# Revit family: E_Actuator_F_MEPcontent_Oventrop_Aktor M ST 2P 3P L Square Law
name_source: partatom
category: Electrical Fixtures
revit_build: Autodesk Revit MEP 2015 (Build: 20140606_1530(x64)
units: mm (PartAtom-declared; Revit-internal decimal feet)

## types (3) — shared parameters
Ambient Temperature = -10 °C up to +55 °C
Black = Color RGB 060-060-060
Content Supplier URL = www.mepcontent.eu
Custom = No
Default Elevation = 1219.2 mm  [stored 4 ft]
Drive = 0–10 V or 4–20 mA
EMCS Version = 2.0
ETIM Article Class = EC011290
Family Version = 10.14
Floating Time = 2 / 4 / 6 s / mm
Grey = Color RGB 100-100-100
Height = 289 mm  [stored 0.948163 ft]
IFCExportAs = IfcActuatorType
IFCExportType = ELECTRICACTUATOR
Length = 230 mm  [stored 0.754593 ft]
MEPcontent Class = ACTUATOR
Manufacturer = Oventrop
Manufacturer URL = http://www.oventrop.com
Max. Piston Stroke = 40 mm
Product Line = Oventrop
Protection = IP 66 according to EN 60529
Revit Version = 2015
Storage Temperature = -10 °C up to +55 °C
URL = www.stabiplan.com
Voltage = 24 V
White = Color RGB 245-245-245
Width = 135.5 mm  [stored 0.444554 ft]

## per-type parameters (varying)
| type | Article Description | Description | GTIN | Manufacturer Art. No. | Max. Fluid Temperature | Number Of Spring Returns | Operating Power | Power Consumption |
| 8030 | Electromotive actuator "Aktor M" "ST/2P/3P L", 24 V, with adapter | Electromotive actuator "Aktor M" "ST/2P/3P L", 24 V, with adapter | 4026755370805 | 1158030 | 120 °C |  | 2500 N | 10 W |
| 8031 | Electromotive actuator "Aktor M" "ST/2P/3P L", 24 V, opening with current off | Electromotive actuator "Aktor M" "ST/2P/3P L", 24 V, opening with current off | 4026755370812 | 1158031 | max. 120 °C | > 4000 | 2000 N | 7.5 W |
| 8032 | Electromotive actuator "Aktor M" "ST/2P/3P L", 24 V, closing with current off | Electromotive actuator "Aktor M" "ST/2P/3P L", 24 V, closing with current off | 4026755399202 | 1158032 | max. 120 °C | > 4000 | 2000 N | 7.5 W |

note: column(s) folded — value = type name in every type: Article Type, Model

note: [stored X ft] marks values corroborated as IEEE doubles in the binary element streams (Revit-internal decimal feet)

## geometry (parser evidence)
native form markers: Sweep x1
no freeform markers — native parametric forms only
